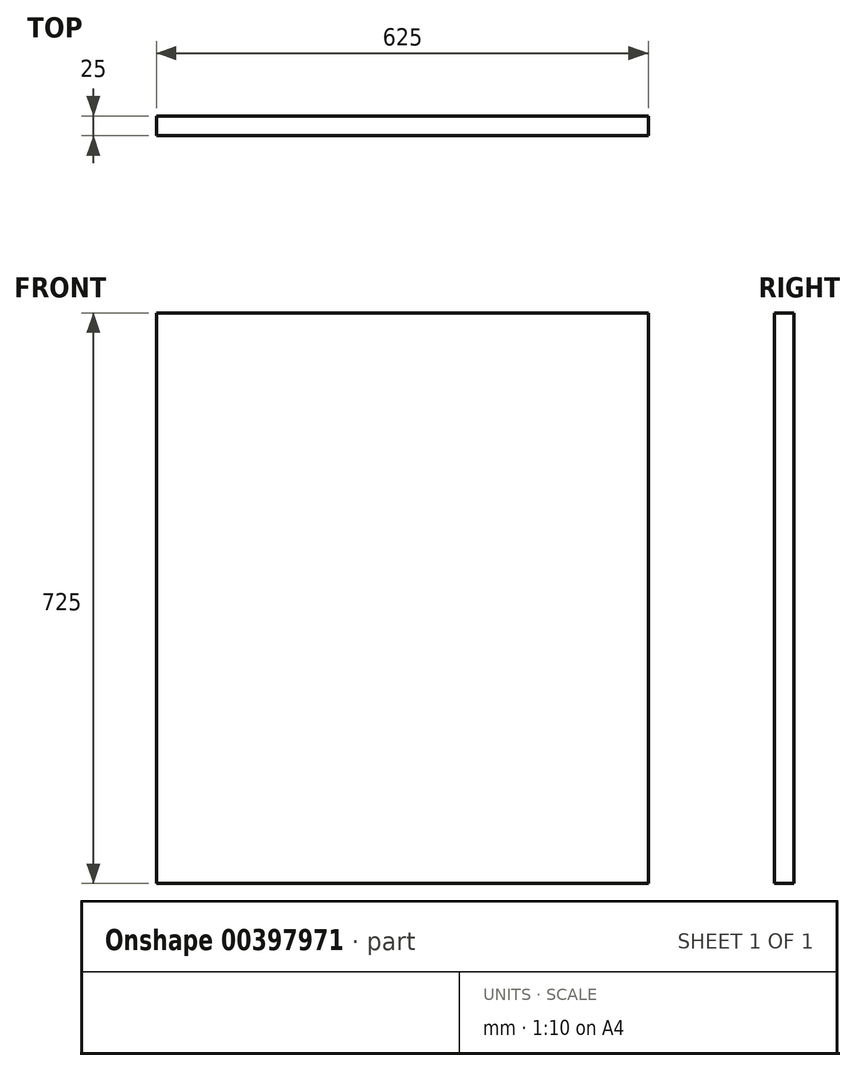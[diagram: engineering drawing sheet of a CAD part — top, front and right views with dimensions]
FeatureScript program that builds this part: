
annotation { "Feature Type Name" : "Feature", "Feature Type Description" : "" }
export const myFeature = defineFeature(function(context is Context, id is Id, definition is map)
    precondition{}
    {
        {
            var Q0;
            Q0=qCreatedBy(makeId("Front.planeOp"),FACE);
            var sketch = newSketch(context, id + "F0", { "sketchPlane" : qUnion([Q0])});
            skLineSegment(sketch, "E0.bottom", {"start": v(-312.5, 362.5) * mm, "end": v(312.5, 362.5) * mm});
            skLineSegment(sketch, "E0.top", {"start": v(-312.5, -362.5) * mm, "end": v(312.5, -362.5) * mm});
            skLineSegment(sketch, "E0.left", {"start": v(-312.5, 362.5) * mm, "end": v(-312.5, -362.5) * mm});
            skLineSegment(sketch, "E0.right", {"start": v(312.5, 362.5) * mm, "end": v(312.5, -362.5) * mm});
            skLineSegment(sketch, "E1", {"start": v(0, 362.5) * mm, "end": v(0, -362.5) * mm, "construction": true});
            skSolve(sketch);
        }
        {
            var Q0;
            Q0=makeQuery(id+"F0.imprint","IMPRINT",FACE,{"disambiguationData":[TD([[makeQuery(id+"F0.imprint","IMPRINT",EDGE,{"derivedFrom":sQuery(id+"F0.wireOp",EDGE,"E0.bottom")}),-1.0]])]});
            extrude(context, id + "F1", {"entities" : qUnion([Q0]), "depth" : 25 * mm});
        }
    });
